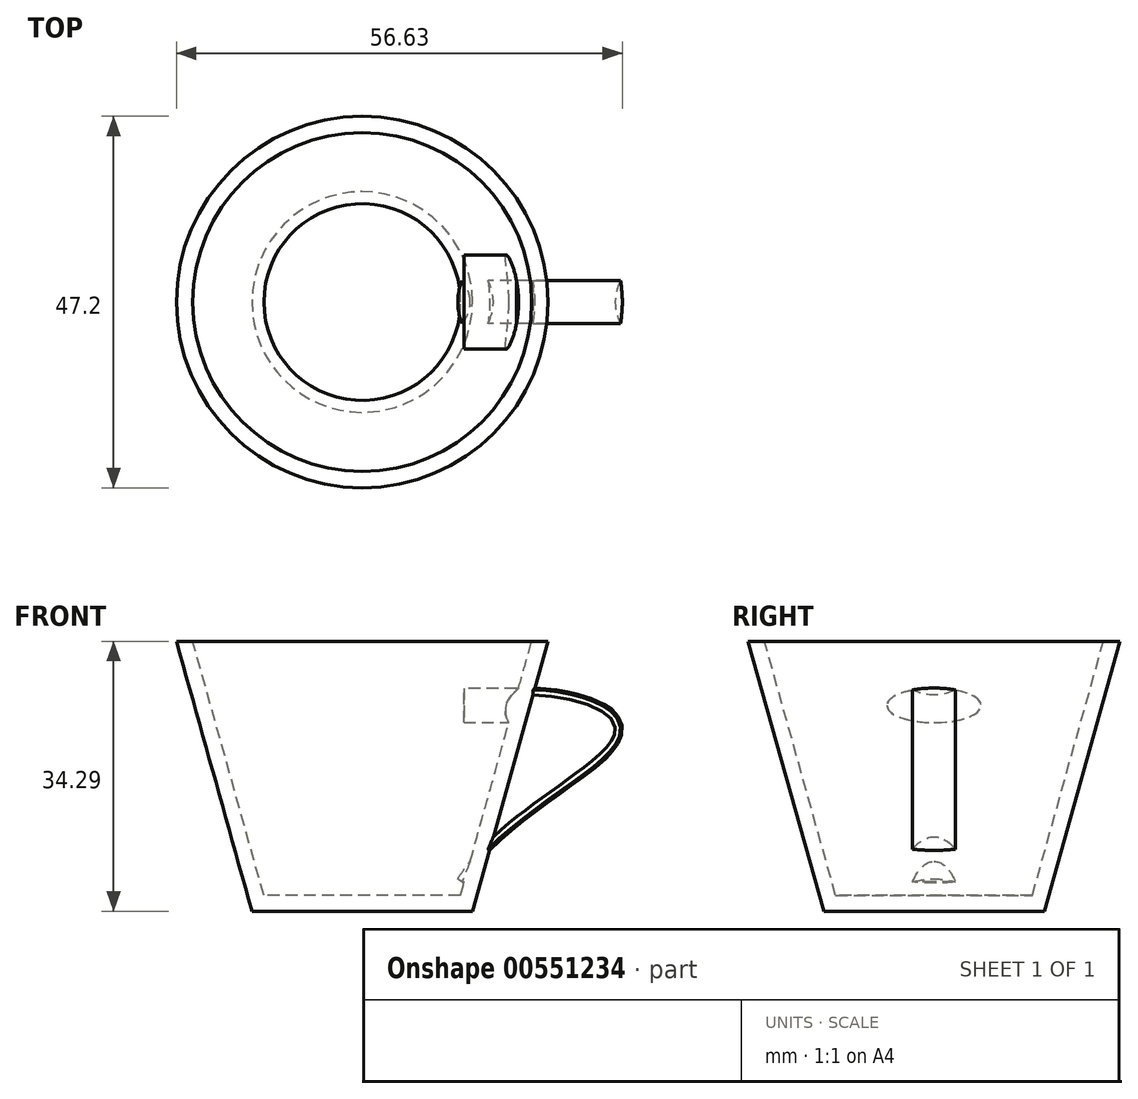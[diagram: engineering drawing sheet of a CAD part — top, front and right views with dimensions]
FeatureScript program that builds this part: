
annotation { "Feature Type Name" : "Feature", "Feature Type Description" : "" }
export const myFeature = defineFeature(function(context is Context, id is Id, definition is map)
    precondition{}
    {
        {
            var Q0;
            Q0=qCreatedBy(makeId("Front.planeOp"),FACE);
            var sketch = newSketch(context, id + "F0", { "sketchPlane" : qUnion([Q0])});
            skLineSegment(sketch, "E0", {"start": v(0, 44.25) * mm, "end": v(23.6, 44.25) * mm});
            skLineSegment(sketch, "E1", {"start": v(23.6, 44.25) * mm, "end": v(14.01, 9.96) * mm});
            skLineSegment(sketch, "E2", {"start": v(14.01, 9.96) * mm, "end": v(0, 9.96) * mm});
            skLineSegment(sketch, "E3", {"start": v(0, 9.96) * mm, "end": v(0, 44.25) * mm});
            skSolve(sketch);
        }
        {
            var Q0;
            Q0=makeQuery(id+"F0.imprint","IMPRINT",FACE,{"disambiguationData":[TD([[makeQuery(id+"F0.imprint","IMPRINT",EDGE,{"derivedFrom":sQuery(id+"F0.wireOp",EDGE,"E0")}),-1.0]])]});
            var Q1;
            Q1=sQuery(id+"F0.wireOp",EDGE,"E3");
            revolve(context, id + "F1", {"entities" : qUnion([Q0]), "axis" : qUnion([Q1]), "revolveType" : RevolveType.FULL});
        }
        {
            var Q0;
            Q0=makeQuery(id+"F1.opRevolve","SWEPT_FACE",FACE,{"disambiguationData":[OSD([sQuery(id+"F0.wireOp",EDGE,"E0")])]});
            shell(context, id + "F2", {"entities" : qUnion([Q0]), "thickness" : 2 * mm});
        }
        {
            var Q0;
            Q0=qCreatedBy(makeId("Front.planeOp"),FACE);
            var sketch = newSketch(context, id + "F3", { "sketchPlane" : qUnion([Q0])});
            skFitSpline(sketch, "E4", {"points": [v(15.74, 35.9) * mm, v(31.61, 33.62) * mm, v(11.8, 14.3) * mm], "startDerivative": vector(24.05, 16.26) * mm, "endDerivative": vector(-29.02, -48.87) * mm});
            skSolve(sketch);
        }
        {
            var Q0;
            Q0=qCreatedBy(makeId("Right.planeOp"),FACE);
            cPlane(context, id + "F4", {"entities" : qUnion([Q0]), "cplaneType" : CPlaneType.OFFSET, "offset" : 12.9 * mm, "width" : 150 * mm, "height" : 150 * mm});
        }
        {
            var Q0;
            Q0=qCreatedBy(id+"F4.planeOp",FACE);
            var sketch = newSketch(context, id + "F5", { "sketchPlane" : qUnion([Q0])});
            skEllipse(sketch, "E5", {"center": v(0, 36.1) * mm, "majorRadius": 5.99 * mm, "minorRadius": 2.18 * mm, "majorAxis": v(-1, 0)});
            skSolve(sketch);
        }
        {
            var Q0;
            Q0 = qSketchRegion(id + "F5", true);
            extrude(context, id + "F6", {"entities" : qUnion([Q0]), "operationType" : NewBodyOperationType.ADD, "depth" : 6.7 * mm, "offsetDistance" : 25 * mm});
        }
        {
            var Q0;
            Q0=makeQuery(id+"F6.opExtrude","CAP_FACE",FACE,{"disambiguationData":[OSD([sQuery(id+"F5.wireOp",EDGE,"E5")])],"isStart":false});
            var Q1;
            Q1=sQuery(id+"F3.wireOp",EDGE,"E4");
            sweep(context, id + "F7", {"operationType" : NewBodyOperationType.ADD, "profiles" : qUnion([Q0]), "path" : qUnion([Q1])});
        }
    });
